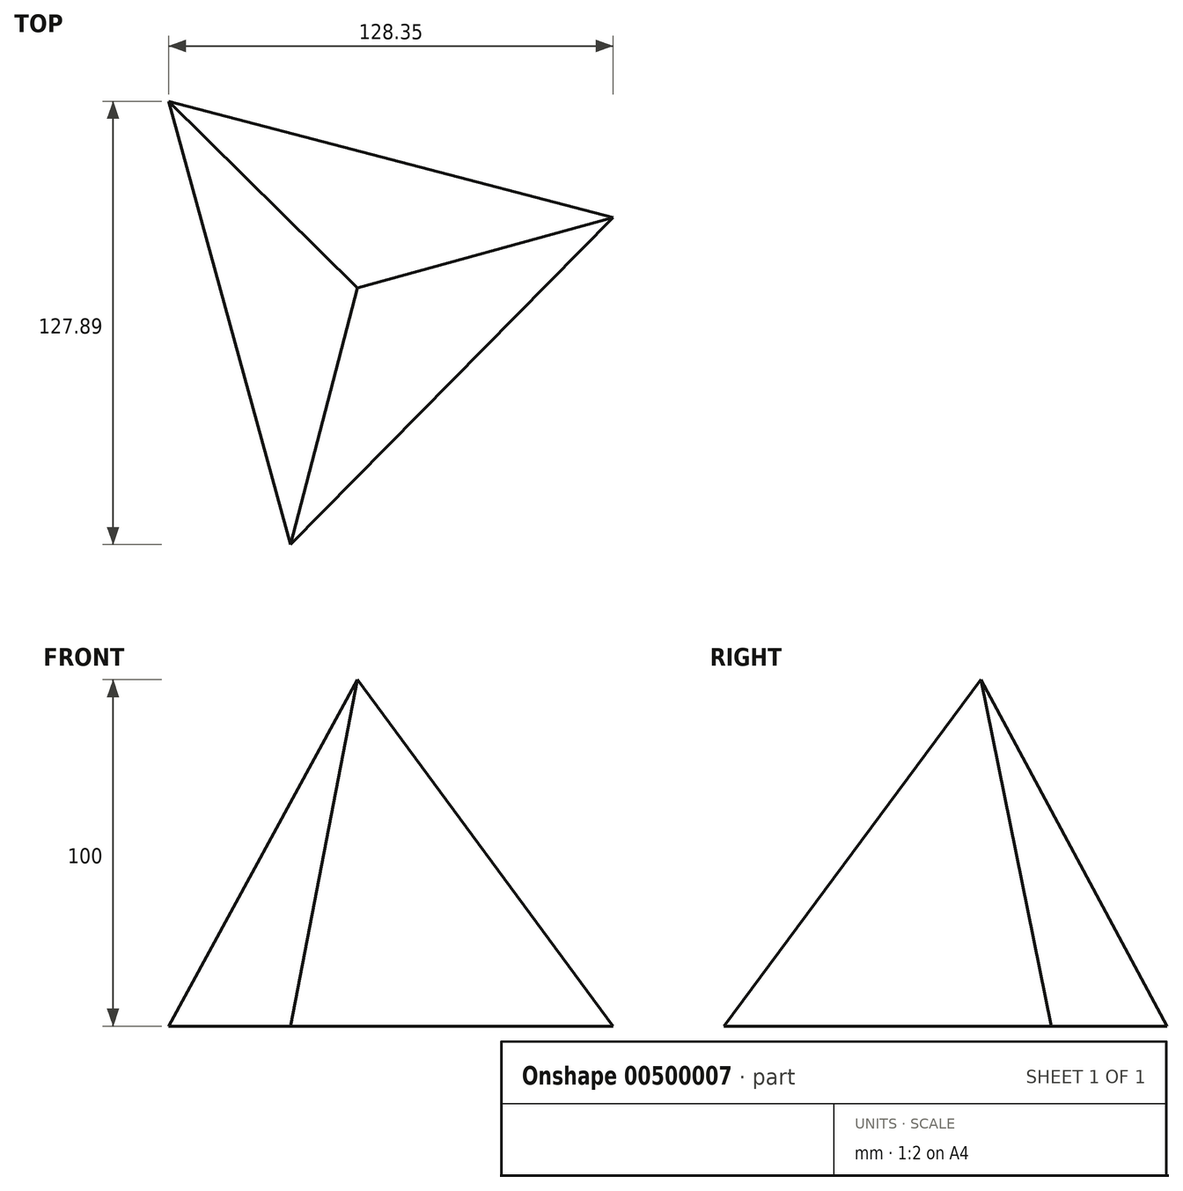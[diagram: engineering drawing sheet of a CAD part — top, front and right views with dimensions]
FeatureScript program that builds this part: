
annotation { "Feature Type Name" : "Feature", "Feature Type Description" : "" }
export const myFeature = defineFeature(function(context is Context, id is Id, definition is map)
    precondition{}
    {
        {
            var Q0;
            Q0=qCreatedBy(makeId("Top.planeOp"),FACE);
            var sketch = newSketch(context, id + "F0", { "sketchPlane" : qUnion([Q0])});
            skCircle(sketch, "E0.cCircle", {"center": v(0, 0) * mm, "radius": 76.58 * mm, "construction": true});
            skLineSegment(sketch, "E0.0", {"start": v(-54.5, 53.8) * mm, "end": v(73.84, 20.3) * mm});
            skLineSegment(sketch, "E0.1", {"start": v(73.84, 20.3) * mm, "end": v(-19.33, -74.1) * mm});
            skLineSegment(sketch, "E0.2", {"start": v(-19.33, -74.1) * mm, "end": v(-54.5, 53.8) * mm});
            skSolve(sketch);
        }
        {
            var Q0;
            Q0=qCreatedBy(makeId("Top.planeOp"),FACE);
            cPlane(context, id + "F1", {"entities" : qUnion([Q0]), "cplaneType" : CPlaneType.OFFSET, "offset" : 100 * mm, "width" : 150 * mm, "height" : 150 * mm});
        }
        {
            var Q0;
            Q0=qCreatedBy(id+"F1.planeOp",FACE);
            var sketch = newSketch(context, id + "F2", { "sketchPlane" : qUnion([Q0])});
            skPoint(sketch, "E1", {"position": v(0, 0) * mm});
            skSolve(sketch);
        }
        {
            var Q0;
            Q0=makeQuery(id+"F0.imprint","IMPRINT",FACE,{"disambiguationData":[TD([[makeQuery(id+"F0.imprint","IMPRINT",EDGE,{"derivedFrom":sQuery(id+"F0.wireOp",EDGE,"E0.0")}),-1.0]])]});
            var Q1;
            Q1=sQuery(id+"F2.wireOp",VERTEX,"E1");
            loft(context, id + "F3", {"sheetProfilesArray" : [{ "sheetProfileEntities" : qUnion([Q0]) }, { "sheetProfileEntities" : qUnion([Q1]) }]});
        }
    });
